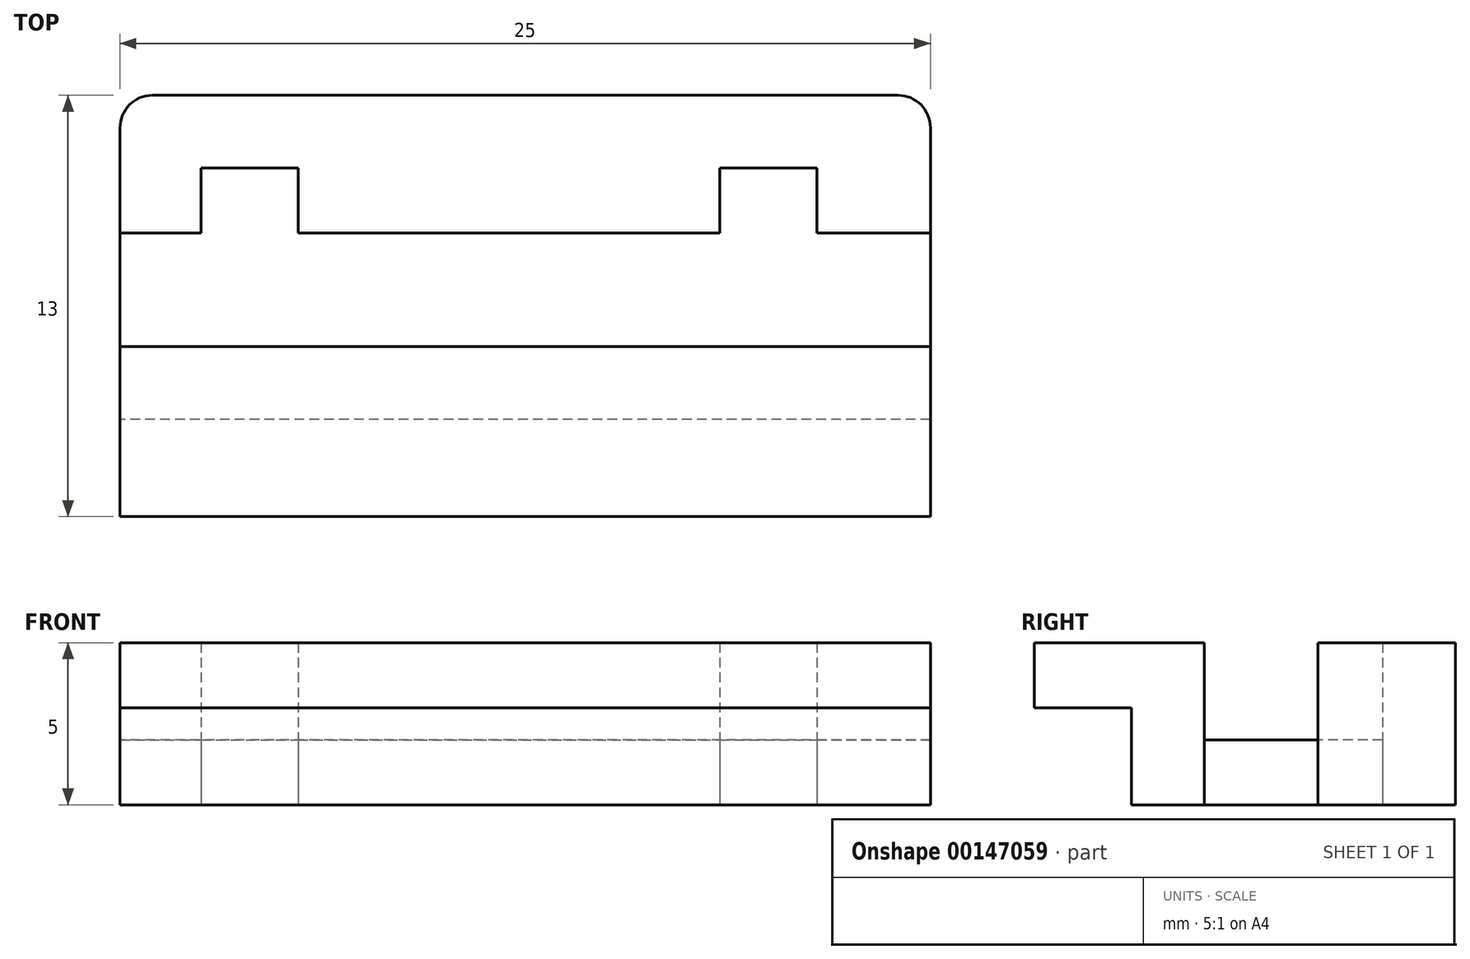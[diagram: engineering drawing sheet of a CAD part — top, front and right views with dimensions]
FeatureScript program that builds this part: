
annotation { "Feature Type Name" : "Feature", "Feature Type Description" : "" }
export const myFeature = defineFeature(function(context is Context, id is Id, definition is map)
    precondition{}
    {
        {
            var Q0;
            Q0=qCreatedBy(makeId("Top.planeOp"),FACE);
            var sketch = newSketch(context, id + "F0", { "sketchPlane" : qUnion([Q0])});
            skLineSegment(sketch, "E0.bottom", {"start": v(-12, 6) * mm, "end": v(13, 6) * mm});
            skLineSegment(sketch, "E0.top", {"start": v(-12, -4) * mm, "end": v(13, -4) * mm});
            skLineSegment(sketch, "E0.left", {"start": v(-12, 6) * mm, "end": v(-12, -4) * mm});
            skLineSegment(sketch, "E0.right", {"start": v(13, 6) * mm, "end": v(13, -4) * mm});
            skLineSegment(sketch, "E1", {"start": v(-12, 1.75) * mm, "end": v(-9.5, 1.75) * mm});
            skLineSegment(sketch, "E2", {"start": v(-9.5, 1.75) * mm, "end": v(-9.5, 3.75) * mm});
            skLineSegment(sketch, "E3", {"start": v(-9.5, 3.75) * mm, "end": v(-6.5, 3.75) * mm});
            skLineSegment(sketch, "E4", {"start": v(-6.5, 3.75) * mm, "end": v(-6.5, 1.75) * mm});
            skLineSegment(sketch, "E5", {"start": v(-6.5, 1.75) * mm, "end": v(6.5, 1.75) * mm});
            skLineSegment(sketch, "E6", {"start": v(6.5, 1.75) * mm, "end": v(6.5, 3.75) * mm});
            skLineSegment(sketch, "E7", {"start": v(6.5, 3.75) * mm, "end": v(9.5, 3.75) * mm});
            skLineSegment(sketch, "E8", {"start": v(9.5, 3.75) * mm, "end": v(9.5, 1.75) * mm});
            skLineSegment(sketch, "E9", {"start": v(9.5, 1.75) * mm, "end": v(13, 1.75) * mm});
            skLineSegment(sketch, "E10", {"start": v(13, 1.75) * mm, "end": v(13, -1.75) * mm});
            skLineSegment(sketch, "E11", {"start": v(13, -1.75) * mm, "end": v(-12, -1.75) * mm});
            skLineSegment(sketch, "E12", {"start": v(-12, -1.75) * mm, "end": v(-12, 1.75) * mm});
            skSolve(sketch);
        }
        {
            var Q0;
            {var subQ0=sQuery(id+"F0.wireOp",EDGE,"E0.bottom");Q0=makeQuery(id+"F0.imprint","IMPRINT",FACE,{"disambiguationData":[TD([[makeQuery(id+"F0.imprint","IMPRINT",EDGE,{"derivedFrom":subQ0}),-1.0]])]});}
            var Q1;
            {var subQ0=sQuery(id+"F0.wireOp",EDGE,"E0.top");Q1=makeQuery(id+"F0.imprint","IMPRINT",FACE,{"disambiguationData":[TD([[makeQuery(id+"F0.imprint","IMPRINT",EDGE,{"derivedFrom":subQ0}),1.0]])]});}
            extrude(context, id + "F1", {"entities" : qUnion([Q0, Q1]), "depth" : 5 * mm});
        }
        {
            var Q0;
            Q0=makeQuery(id+"F0.imprint","IMPRINT",FACE,{"disambiguationData":[TD([[makeQuery(id+"F0.imprint","IMPRINT",EDGE,{"derivedFrom":sQuery(id+"F0.wireOp",EDGE,"E1")}),-1.0]])]});
            extrude(context, id + "F2", {"entities" : qUnion([Q0]), "depth" : 2 * mm});
        }
        {
            var Q0;
            Q0=makeQuery(id+"F1.opExtrude","SWEPT_EDGE",EDGE,{"disambiguationData":[OSD([sQuery(id+"F0.wireOp",EDGE,"E0.bottom"),sQuery(id+"F0.wireOp",EDGE,"E0.right")])]});
            var Q1;
            Q1=makeQuery(id+"F1.opExtrude","SWEPT_EDGE",EDGE,{"disambiguationData":[OSD([sQuery(id+"F0.wireOp",EDGE,"E0.bottom"),sQuery(id+"F0.wireOp",EDGE,"E0.left")])]});
            fillet(context, id + "F3", {"entities" : qUnion([Q0, Q1]), "radius" : 1 * mm, "tangentPropagation" : true, "allowEdgeOverflow" : false});
        }
        {
            var Q0;
            Q0=makeQuery(id+"F1.opExtrude","SWEPT_FACE",FACE,{"disambiguationData":[OSD([sQuery(id+"F0.wireOp",EDGE,"E0.top")])]});
            var sketch = newSketch(context, id + "F4", { "sketchPlane" : qUnion([Q0])});
            skLineSegment(sketch, "E13.bottom", {"start": v(13, 0) * mm, "end": v(-12, 0) * mm});
            skLineSegment(sketch, "E13.top", {"start": v(13, 5) * mm, "end": v(-12, 5) * mm});
            skLineSegment(sketch, "E13.left", {"start": v(13, 0) * mm, "end": v(13, 5) * mm});
            skLineSegment(sketch, "E13.right", {"start": v(-12, 0) * mm, "end": v(-12, 5) * mm});
            skLineSegment(sketch, "E14", {"start": v(13, 3) * mm, "end": v(-12, 3) * mm});
            skSolve(sketch);
        }
        {
            var Q0;
            {var subQ0=sQuery(id+"F4.wireOp",EDGE,"E13.top");Q0=makeQuery(id+"F4.imprint","IMPRINT",FACE,{"disambiguationData":[TD([[makeQuery(id+"F4.imprint","IMPRINT",EDGE,{"derivedFrom":subQ0}),-1.0]])]});}
            extrude(context, id + "F5", {"entities" : qUnion([Q0]), "operationType" : NewBodyOperationType.ADD, "depth" : 3 * mm});
        }
    });
